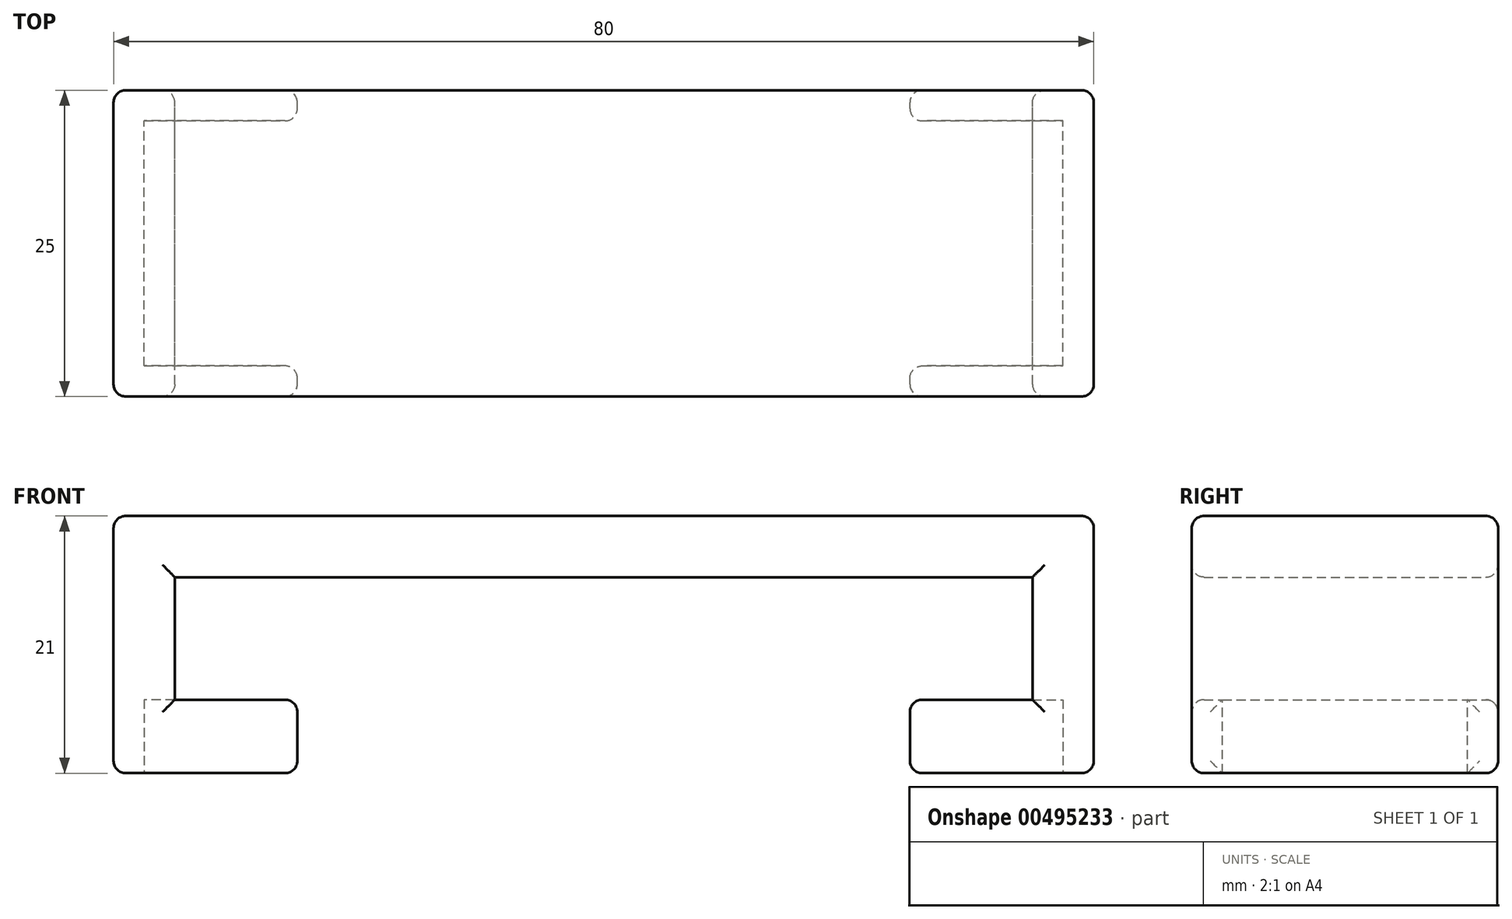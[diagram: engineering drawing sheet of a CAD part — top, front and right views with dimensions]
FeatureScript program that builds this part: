
annotation { "Feature Type Name" : "Feature", "Feature Type Description" : "" }
export const myFeature = defineFeature(function(context is Context, id is Id, definition is map)
    precondition{}
    {
        {
            var Q0;
            Q0=qCreatedBy(makeId("Front.planeOp"),FACE);
            var sketch = newSketch(context, id + "F0", { "sketchPlane" : qUnion([Q0])});
            skLineSegment(sketch, "E0", {"start": v(-48.08, 33.83) * mm, "end": v(21.92, 33.83) * mm});
            skLineSegment(sketch, "E1", {"start": v(21.92, 33.83) * mm, "end": v(21.92, 23.83) * mm});
            skLineSegment(sketch, "E2", {"start": v(-48.08, 33.83) * mm, "end": v(-48.08, 23.83) * mm});
            skLineSegment(sketch, "E3.0", {"start": v(-53.08, 38.83) * mm, "end": v(-53.08, 17.83) * mm});
            skLineSegment(sketch, "E3.1", {"start": v(-53.08, 38.83) * mm, "end": v(26.92, 38.83) * mm});
            skLineSegment(sketch, "E3.2", {"start": v(26.92, 38.83) * mm, "end": v(26.92, 17.83) * mm});
            skLineSegment(sketch, "E4", {"start": v(-53.08, 17.83) * mm, "end": v(-48.08, 17.83) * mm});
            skLineSegment(sketch, "E5", {"start": v(21.92, 17.83) * mm, "end": v(26.92, 17.83) * mm});
            skLineSegment(sketch, "E6", {"start": v(-48.08, 17.83) * mm, "end": v(-38.08, 17.83) * mm});
            skLineSegment(sketch, "E7", {"start": v(-38.08, 17.83) * mm, "end": v(-38.08, 23.83) * mm});
            skLineSegment(sketch, "E8", {"start": v(-38.08, 23.83) * mm, "end": v(-48.08, 23.83) * mm});
            skLineSegment(sketch, "E9", {"start": v(21.92, 17.83) * mm, "end": v(11.92, 17.83) * mm});
            skLineSegment(sketch, "E10", {"start": v(11.92, 17.83) * mm, "end": v(11.92, 23.83) * mm});
            skLineSegment(sketch, "E11", {"start": v(11.92, 23.83) * mm, "end": v(21.92, 23.83) * mm});
            skSolve(sketch);
        }
        {
            var Q0;
            Q0 = qSketchRegion(id + "F0", true);
            extrude(context, id + "F1", {"entities" : qUnion([Q0]), "depth" : 25 * mm});
        }
        {
            var Q0;
            Q0=makeQuery(id+"F1.opExtrude","SWEPT_FACE",FACE,{"disambiguationData":[OSD([sQuery(id+"F0.wireOp",EDGE,"E8")])]});
            var Q1;
            Q1=makeQuery(id+"F1.opExtrude","SWEPT_FACE",FACE,{"disambiguationData":[OSD([sQuery(id+"F0.wireOp",EDGE,"E7")])]});
            var Q2;
            Q2=makeQuery(id+"F1.opExtrude","SWEPT_FACE",FACE,{"disambiguationData":[OSD([sQuery(id+"F0.wireOp",EDGE,"E4"),sQuery(id+"F0.wireOp",EDGE,"E6")])]});
            var Q3;
            Q3=makeQuery(id+"F1.opExtrude","SWEPT_FACE",FACE,{"disambiguationData":[OSD([sQuery(id+"F0.wireOp",EDGE,"E5"),sQuery(id+"F0.wireOp",EDGE,"E9")])]});
            var Q4;
            Q4=makeQuery(id+"F1.opExtrude","SWEPT_FACE",FACE,{"disambiguationData":[OSD([sQuery(id+"F0.wireOp",EDGE,"E10")])]});
            var Q5;
            Q5=makeQuery(id+"F1.opExtrude","SWEPT_FACE",FACE,{"disambiguationData":[OSD([sQuery(id+"F0.wireOp",EDGE,"E11")])]});
            shell(context, id + "F2", {"entities" : qUnion([Q0, Q1, Q2, Q3, Q4, Q5]), "thickness" : 2.5 * mm});
        }
        {
            var Q0;
            Q0=makeQuery(id+"F1.opExtrude","SWEPT_FACE",FACE,{"disambiguationData":[OSD([sQuery(id+"F0.wireOp",EDGE,"E7")])]});
            var Q1;
            Q1=makeQuery(id+"F2.opShell","OFFSET_FACE",FACE,{"disambiguationData":[OSD([sQuery(id+"F0.wireOp",EDGE,"E7")])]});
            var Q2;
            Q2=makeQuery(id+"F1.opExtrude","SWEPT_FACE",FACE,{"disambiguationData":[OSD([sQuery(id+"F0.wireOp",EDGE,"E10")])]});
            var Q3;
            Q3=makeQuery(id+"F2.opShell","OFFSET_FACE",FACE,{"disambiguationData":[OSD([sQuery(id+"F0.wireOp",EDGE,"E10")])]});
            var Q4;
            Q4=makeQuery(id+"F1.opExtrude","CAP_FACE",FACE,{"disambiguationData":[OSD([sQuery(id+"F0.wireOp",EDGE,"E0"),sQuery(id+"F0.wireOp",EDGE,"E1"),sQuery(id+"F0.wireOp",EDGE,"E2"),sQuery(id+"F0.wireOp",EDGE,"E3.0"),sQuery(id+"F0.wireOp",EDGE,"E3.1"),sQuery(id+"F0.wireOp",EDGE,"E3.2"),sQuery(id+"F0.wireOp",EDGE,"E4"),sQuery(id+"F0.wireOp",EDGE,"E5"),sQuery(id+"F0.wireOp",EDGE,"E6"),sQuery(id+"F0.wireOp",EDGE,"E7"),sQuery(id+"F0.wireOp",EDGE,"E8"),sQuery(id+"F0.wireOp",EDGE,"E9"),sQuery(id+"F0.wireOp",EDGE,"E10"),sQuery(id+"F0.wireOp",EDGE,"E11")])],"isStart":true});
            var Q5;
            Q5=makeQuery(id+"F1.opExtrude","SWEPT_FACE",FACE,{"disambiguationData":[OSD([sQuery(id+"F0.wireOp",EDGE,"E3.2")])]});
            var Q6;
            Q6=makeQuery(id+"F1.opExtrude","CAP_FACE",FACE,{"disambiguationData":[OSD([sQuery(id+"F0.wireOp",EDGE,"E0"),sQuery(id+"F0.wireOp",EDGE,"E1"),sQuery(id+"F0.wireOp",EDGE,"E2"),sQuery(id+"F0.wireOp",EDGE,"E3.0"),sQuery(id+"F0.wireOp",EDGE,"E3.1"),sQuery(id+"F0.wireOp",EDGE,"E3.2"),sQuery(id+"F0.wireOp",EDGE,"E4"),sQuery(id+"F0.wireOp",EDGE,"E5"),sQuery(id+"F0.wireOp",EDGE,"E6"),sQuery(id+"F0.wireOp",EDGE,"E7"),sQuery(id+"F0.wireOp",EDGE,"E8"),sQuery(id+"F0.wireOp",EDGE,"E9"),sQuery(id+"F0.wireOp",EDGE,"E10"),sQuery(id+"F0.wireOp",EDGE,"E11")])],"isStart":false});
            var Q7;
            Q7=makeQuery(id+"F1.opExtrude","SWEPT_FACE",FACE,{"disambiguationData":[OSD([sQuery(id+"F0.wireOp",EDGE,"E3.0")])]});
            fillet(context, id + "F3", {"entities" : qUnion([Q0, Q1, Q2, Q3, Q4, Q5, Q6, Q7]), "radius" : 1 * mm, "tangentPropagation" : true, "allowEdgeOverflow" : false});
        }
    });
